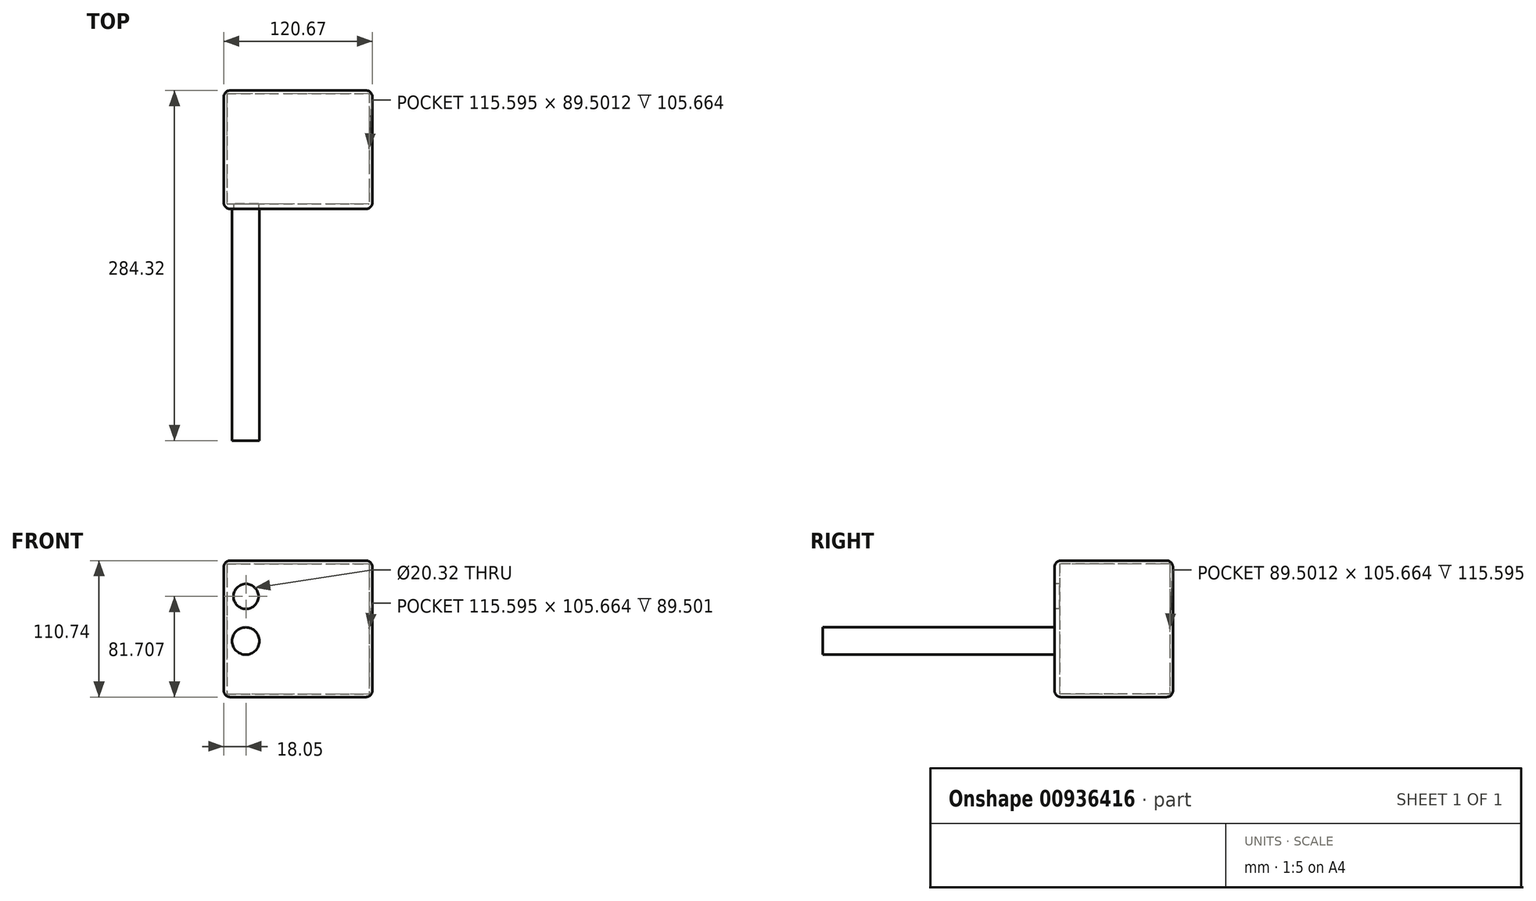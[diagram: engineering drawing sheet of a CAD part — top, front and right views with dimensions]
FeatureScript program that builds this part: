
annotation { "Feature Type Name" : "Feature", "Feature Type Description" : "" }
export const myFeature = defineFeature(function(context is Context, id is Id, definition is map)
    precondition{}
    {
        {
            var Q0;
            Q0=qCreatedBy(makeId("Top.planeOp"),FACE);
            var sketch = newSketch(context, id + "F0", { "sketchPlane" : qUnion([Q0])});
            skLineSegment(sketch, "E0.bottom", {"start": v(-62.84, 50.7) * mm, "end": v(57.83, 50.7) * mm});
            skLineSegment(sketch, "E0.top", {"start": v(-62.84, -45.4) * mm, "end": v(57.83, -45.4) * mm});
            skLineSegment(sketch, "E0.left", {"start": v(-62.84, 50.7) * mm, "end": v(-62.84, -45.4) * mm});
            skLineSegment(sketch, "E0.right", {"start": v(57.83, 50.7) * mm, "end": v(57.83, -45.4) * mm});
            skSolve(sketch);
        }
        {
            var Q0;
            Q0=makeQuery(id+"F0.imprint","IMPRINT",FACE,{"disambiguationData":[TD([[makeQuery(id+"F0.imprint","IMPRINT",EDGE,{"derivedFrom":sQuery(id+"F0.wireOp",EDGE,"E0.bottom")}),-1.0]])]});
            extrude(context, id + "F1", {"entities" : qUnion([Q0]), "depth" : 110.74 * mm, "offsetDistance" : 25.4 * mm});
        }
        {
            var Q0;
            Q0=makeQuery(id+"F1.opExtrude","SWEPT_FACE",FACE,{"disambiguationData":[OSD([sQuery(id+"F0.wireOp",EDGE,"E0.top")])]});
            shell(context, id + "F2", {"entities" : qUnion([Q0]), "thickness" : 2.54 * mm});
        }
        {
            var Q0;
            Q0=makeQuery(id+"F1.opExtrude","SWEPT_FACE",FACE,{"disambiguationData":[OSD([sQuery(id+"F0.wireOp",EDGE,"E0.top")])]});
            var sketch = newSketch(context, id + "F3", { "sketchPlane" : qUnion([Q0])});
            skLineSegment(sketch, "E1.bottom", {"start": v(-60.3, 108.2) * mm, "end": v(55.3, 108.2) * mm});
            skLineSegment(sketch, "E1.top", {"start": v(-60.3, 2.54) * mm, "end": v(55.3, 2.54) * mm});
            skLineSegment(sketch, "E1.left", {"start": v(-60.3, 108.2) * mm, "end": v(-60.3, 2.54) * mm});
            skLineSegment(sketch, "E1.right", {"start": v(55.3, 108.2) * mm, "end": v(55.3, 2.54) * mm});
            skSolve(sketch);
        }
        {
            var Q0;
            Q0=makeQuery(id+"F3.imprint","IMPRINT",FACE,{"disambiguationData":[TD([[makeQuery(id+"F3.imprint","IMPRINT",EDGE,{"derivedFrom":sQuery(id+"F3.wireOp",EDGE,"E1.bottom")}),-1.0]])]});
            extrude(context, id + "F4", {"entities" : qUnion([Q0]), "operationType" : NewBodyOperationType.ADD, "oppositeDirection" : true, "depth" : 4.06 * mm, "offsetDistance" : 25.4 * mm});
        }
        {
            var Q0;
            Q0=makeQuery(id+"F4.boolean.opBoolean","MERGE",FACE,{"derivedFrom":[makeQuery(id+"F1.opExtrude","SWEPT_FACE",FACE,{"disambiguationData":[OSD([sQuery(id+"F0.wireOp",EDGE,"E0.top")])]}),makeQuery(id+"F4.opExtrude","CAP_FACE",FACE,{"disambiguationData":[OSD([sQuery(id+"F3.wireOp",EDGE,"E1.bottom"),sQuery(id+"F3.wireOp",EDGE,"E1.top"),sQuery(id+"F3.wireOp",EDGE,"E1.left"),sQuery(id+"F3.wireOp",EDGE,"E1.right")])],"isStart":true})]});
            var sketch = newSketch(context, id + "F5", { "sketchPlane" : qUnion([Q0])});
            skCircle(sketch, "E2", {"center": v(-44.8, 81.7) * mm, "radius": 11.53 * mm});
            skSolve(sketch);
        }
        {
            var Q0;
            Q0=sQuery(id+"F5.wireOp",VERTEX,"E2.center");
            var Q1;
            Q1=makeQuery(id+"F1.opExtrude","SWEPT_BODY",BODY,{"disambiguationData":[OSD([sQuery(id+"F0.wireOp",EDGE,"E0.bottom"),sQuery(id+"F0.wireOp",EDGE,"E0.top"),sQuery(id+"F0.wireOp",EDGE,"E0.left"),sQuery(id+"F0.wireOp",EDGE,"E0.right")])]});
            hole(context, id + "F6", {"style" : HoleStyle.SIMPLE, "endStyle" : HoleEndStyle.BLIND, "holeDiameter" : 20.32 * mm, "majorDiameter" : 6.35 * mm, "holeDepth" : 5.08 * mm, "isTappedThrough" : true, "tappedDepth" : 12.7 * mm, "tapClearance" : 3, "locations" : qUnion([Q0]), "scope" : qUnion([Q1])});
        }
        {
            var Q0;
            Q0=makeQuery(id+"F4.boolean.opBoolean","MERGE",FACE,{"derivedFrom":[makeQuery(id+"F1.opExtrude","SWEPT_FACE",FACE,{"disambiguationData":[OSD([sQuery(id+"F0.wireOp",EDGE,"E0.top")])]}),makeQuery(id+"F4.opExtrude","CAP_FACE",FACE,{"disambiguationData":[OSD([sQuery(id+"F3.wireOp",EDGE,"E1.bottom"),sQuery(id+"F3.wireOp",EDGE,"E1.top"),sQuery(id+"F3.wireOp",EDGE,"E1.left"),sQuery(id+"F3.wireOp",EDGE,"E1.right")])],"isStart":true})]});
            var sketch = newSketch(context, id + "F7", { "sketchPlane" : qUnion([Q0])});
            skCircle(sketch, "E3", {"center": v(-45, 45.47) * mm, "radius": 11.08 * mm});
            skCircle(sketch, "E4", {"center": v(-17.72, 50.26) * mm, "radius": 9.7 * mm});
            skCircle(sketch, "E5", {"center": v(-34.44, 20.9) * mm, "radius": 8.74 * mm});
            skCircle(sketch, "E6", {"center": v(14.53, 42.6) * mm, "radius": 8.07 * mm});
            skSolve(sketch);
        }
        {
            var Q0;
            Q0=makeQuery(id+"F7.imprint","IMPRINT",FACE,{"disambiguationData":[TD([[makeQuery(id+"F7.imprint","IMPRINT",EDGE,{"derivedFrom":sQuery(id+"F7.wireOp",EDGE,"E3")}),1.0]])]});
            extrude(context, id + "F8", {"entities" : qUnion([Q0]), "operationType" : NewBodyOperationType.ADD, "depth" : 188.21 * mm, "offsetDistance" : 25.4 * mm});
        }
        {
            var Q0;
            Q0=makeQuery(id+"F1.opExtrude","CAP_EDGE",EDGE,{"disambiguationData":[OSD([sQuery(id+"F0.wireOp",EDGE,"E0.top")])],"isStart":false});
            var Q1;
            Q1=makeQuery(id+"F1.opExtrude","SWEPT_EDGE",EDGE,{"disambiguationData":[OSD([sQuery(id+"F0.wireOp",EDGE,"E0.top"),sQuery(id+"F0.wireOp",EDGE,"E0.right")])]});
            var Q2;
            Q2=makeQuery(id+"F1.opExtrude","SWEPT_EDGE",EDGE,{"disambiguationData":[OSD([sQuery(id+"F0.wireOp",EDGE,"E0.bottom"),sQuery(id+"F0.wireOp",EDGE,"E0.right")])]});
            var Q3;
            Q3=makeQuery(id+"F1.opExtrude","CAP_EDGE",EDGE,{"disambiguationData":[OSD([sQuery(id+"F0.wireOp",EDGE,"E0.right")])],"isStart":false});
            var Q4;
            Q4=makeQuery(id+"F1.opExtrude","CAP_EDGE",EDGE,{"disambiguationData":[OSD([sQuery(id+"F0.wireOp",EDGE,"E0.bottom")])],"isStart":false});
            var Q5;
            Q5=makeQuery(id+"F1.opExtrude","CAP_EDGE",EDGE,{"disambiguationData":[OSD([sQuery(id+"F0.wireOp",EDGE,"E0.left")])],"isStart":false});
            var Q6;
            Q6=makeQuery(id+"F1.opExtrude","SWEPT_EDGE",EDGE,{"disambiguationData":[OSD([sQuery(id+"F0.wireOp",EDGE,"E0.top"),sQuery(id+"F0.wireOp",EDGE,"E0.left")])]});
            var Q7;
            Q7=makeQuery(id+"F1.opExtrude","CAP_EDGE",EDGE,{"disambiguationData":[OSD([sQuery(id+"F0.wireOp",EDGE,"E0.top")])],"isStart":true});
            var Q8;
            Q8=makeQuery(id+"F1.opExtrude","CAP_EDGE",EDGE,{"disambiguationData":[OSD([sQuery(id+"F0.wireOp",EDGE,"E0.right")])],"isStart":true});
            var Q9;
            Q9=makeQuery(id+"F1.opExtrude","CAP_EDGE",EDGE,{"disambiguationData":[OSD([sQuery(id+"F0.wireOp",EDGE,"E0.bottom")])],"isStart":true});
            var Q10;
            Q10=makeQuery(id+"F1.opExtrude","CAP_EDGE",EDGE,{"disambiguationData":[OSD([sQuery(id+"F0.wireOp",EDGE,"E0.left")])],"isStart":true});
            var Q11;
            Q11=makeQuery(id+"F1.opExtrude","SWEPT_EDGE",EDGE,{"disambiguationData":[OSD([sQuery(id+"F0.wireOp",EDGE,"E0.bottom"),sQuery(id+"F0.wireOp",EDGE,"E0.left")])]});
            fillet(context, id + "F9", {"entities" : qUnion([Q0, Q1, Q2, Q3, Q4, Q5, Q6, Q7, Q8, Q9, Q10, Q11]), "radius" : 5.08 * mm, "tangentPropagation" : true, "allowEdgeOverflow" : false});
        }
    });
